# Revit family: GGU_Ver.2.5
name_source: partatom
category: Windows
revit_build: Autodesk Revit Architecture 2014 (Build: 20130308_1515(x64)
units: mm (PartAtom-declared; Revit-internal decimal feet)

## types (1)
- GGU size 550x780 (CK02)
    2d details = http://www.velux.co.uk
    AcousticRating = 35
    Air permeability Class = 4
    Allowed Roof Slope = 15°-90°
    Angle = 0.00°
    Apron Material = Two layers of aluminium
    Assembly Code = B3020110
    Colour = Aluminium. Color NCS 7500-N
    Count = 1
    Description = http://www.velux.co.uk
    Disclaimer = When installing VELUX roof windows the costumer must make sure to meet local applicable building and fire requirements. VELUX shall not be liable for the objects/drawings and the constructional quality of the installation. Please contact VELUX for technical specifications of VELUX roof windows, flashings, installations products and internal/external accessories.
    DocumentReference = http://www.professional.velux.co.uk
    Documentation = http://www.professional.velux.co.uk
    Emergency Exit = No
    Features = Pivot hung roof window
    Finish = Polyurethane color NCS 0500-N
    FireRating = E
    Function = Pivot hung roof window
    Glazing = Standard, extra solar gain (--70)
    Height = 780 mm  [stored 2.55906 ft]
    Installation instructions = http://www.velux.co.uk
    IsExternal = Yes
    Light transmittance = 0.8
    Manufacturer = VELUX A/S
    Manufacturer URL = www.VELUX.com
    Material = Aluminium. Color NCS 7500-N
    Material External = Aluminium. Color NCS 7500-N
    Material Internal = Polyurethane color NCS 0500-N
    Model = New Generation - GGU
    ModelReference = GGU size 550x780 (CK02)
    NominalHeight = 780
    NominalWidth = 550
    Offset from Roof = 169 mm  [stored 0.554462 ft]
    Open Window = No
    Opening Lines = Yes
    Operation Mode = Manual
    Panel Offset = -119 mm  [stored -0.39042 ft]
    PerimeterGlazing m = 1.9146
    PerimeterWindow m = 2.66
    Placement Height = 0 mm  [stored 0 ft]
    Product certification = www.velux.com/ce
    ReferenceStandard = www.velux.com/ce
    Roof Slope = 45.00°
    Shape = Rectangular
    Size = GGU size 550x780 (CK02)
    SmokeStop = No
    Sound Insulation db = 35
    Square Reveal Length = 150 mm
    Technical description = http://www.velux.co.uk
    Thermal Resistance (R) = 0.7692307692
    ThermalBridge(Installation) W/mK = 0.09
    ThermalBridge(glazing) W/mK = 0.055
    ThermalTransmittance = 1.3
    URL = www.VELUX.com
    Ultraviolet Transmittance = 0.05
    Ventilations flap areal mm2 = 2600
    Warranty Years = 5 (10 with BDX)
    Water Tightness Class = 9A
    Width = 550 mm  [stored 1.80446 ft]
    Window Opening Angle = 0.00°
    Within Standard Sizes = Yes
    g-value = 0.63

note: [stored X ft] marks values corroborated as IEEE doubles in the binary element streams (Revit-internal decimal feet)

## geometry (parser evidence)
native form markers: Blend x21, Sweep x5
no freeform markers — native parametric forms only
